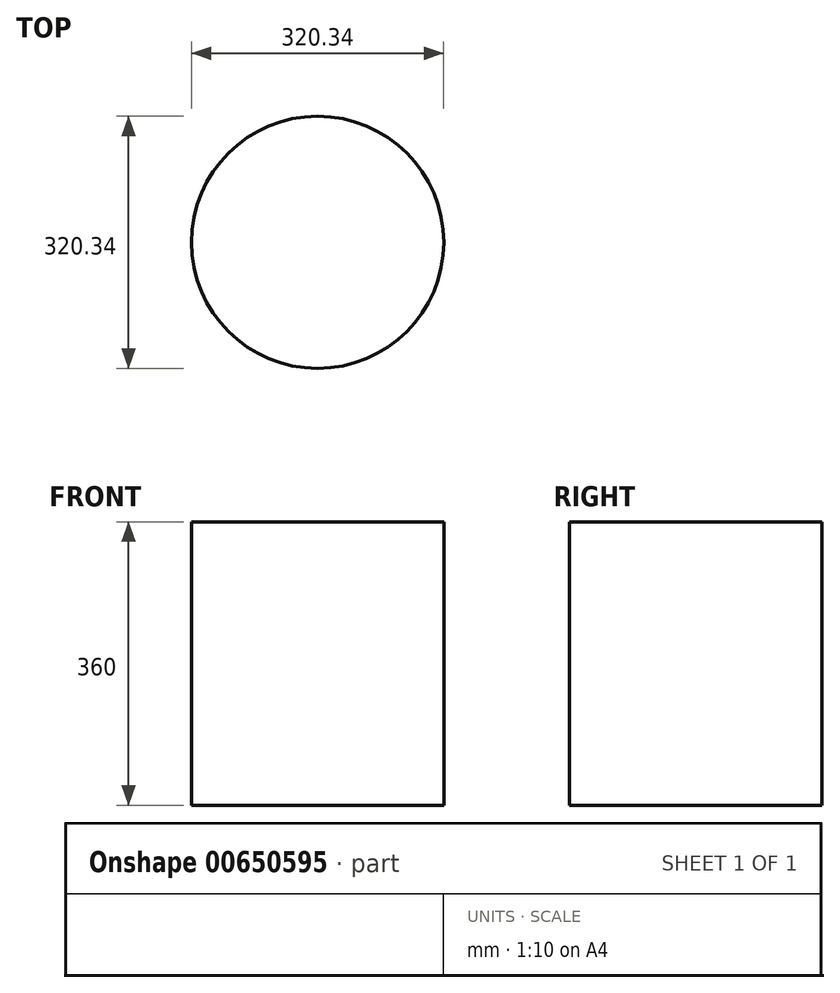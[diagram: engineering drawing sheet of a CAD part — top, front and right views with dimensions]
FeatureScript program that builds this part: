
annotation { "Feature Type Name" : "Feature", "Feature Type Description" : "" }
export const myFeature = defineFeature(function(context is Context, id is Id, definition is map)
    precondition{}
    {
        {
            var Q0;
            Q0=qCreatedBy(makeId("Top.planeOp"),FACE);
            var sketch = newSketch(context, id + "F0", { "sketchPlane" : qUnion([Q0])});
            skCircle(sketch, "E0", {"center": v(0, 0) * mm, "radius": 160.17 * mm});
            skSolve(sketch);
        }
        {
            var Q0;
            Q0=makeQuery(id+"F0.imprint","IMPRINT",FACE,{"disambiguationData":[TD([[makeQuery(id+"F0.imprint","IMPRINT",EDGE,{"derivedFrom":sQuery(id+"F0.wireOp",EDGE,"E0")}),1.0]])]});
            extrude(context, id + "F1", {"entities" : qUnion([Q0]), "depth" : 360 * mm, "offsetDistance" : 25 * mm});
        }
    });
